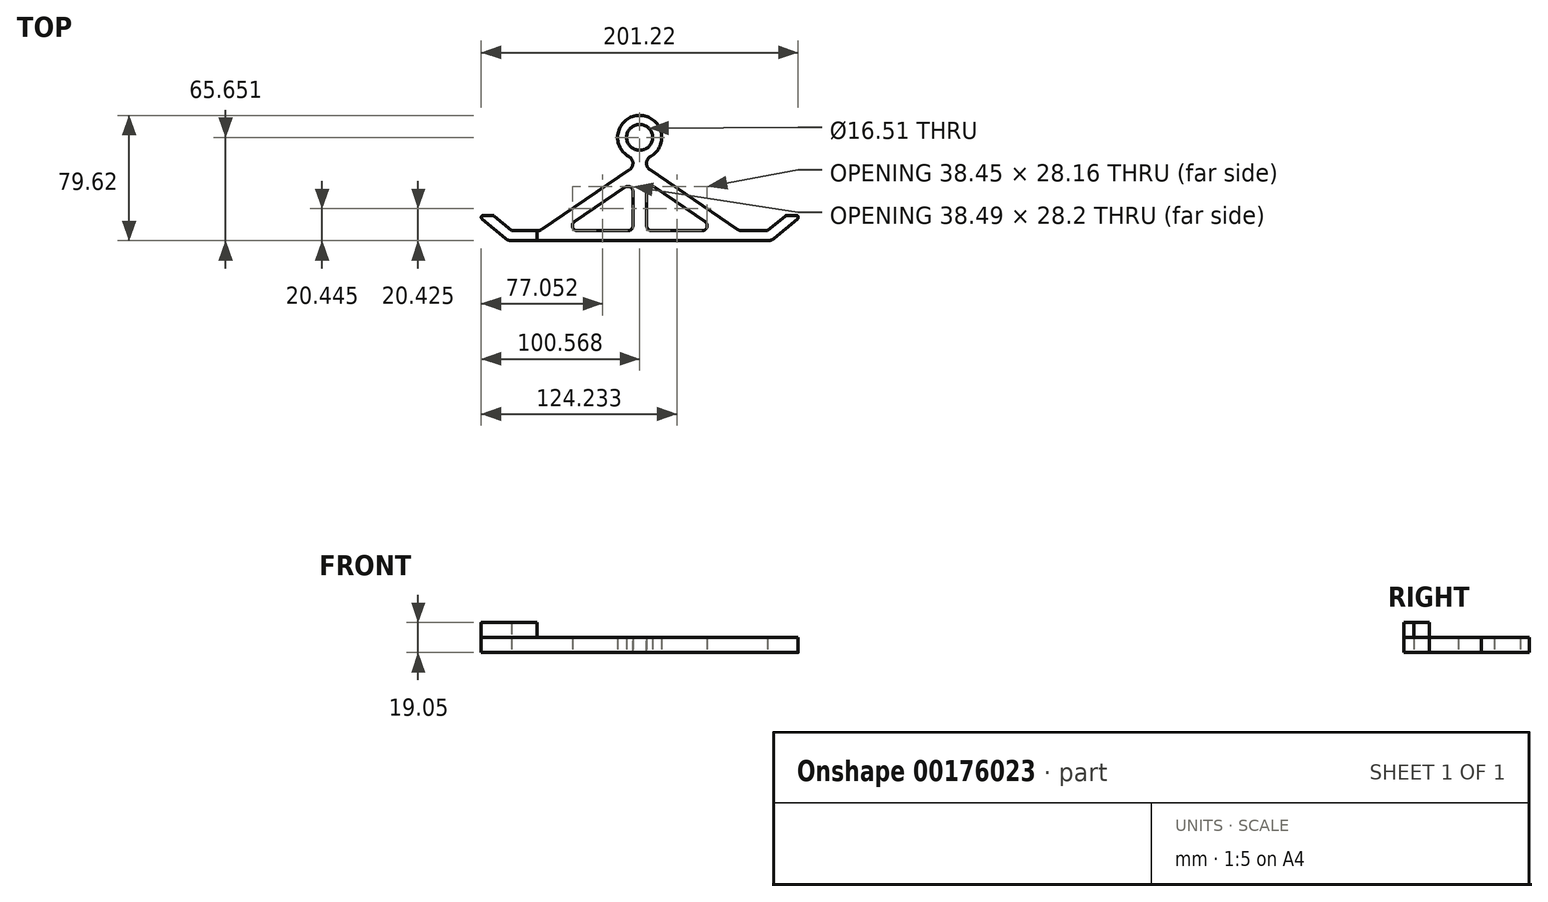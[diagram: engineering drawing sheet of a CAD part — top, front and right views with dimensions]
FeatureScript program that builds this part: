
annotation { "Feature Type Name" : "Feature", "Feature Type Description" : "" }
export const myFeature = defineFeature(function(context is Context, id is Id, definition is map)
    precondition{}
    {
        {
            var Q0;
            Q0=qCreatedBy(makeId("Top.planeOp"),FACE);
            var sketch = newSketch(context, id + "F0", { "sketchPlane" : qUnion([Q0])});
            skPoint(sketch, "E0", {"position": v(0, 0) * mm});
            skLineSegment(sketch, "E1.bottom", {"start": v(-4.4, 50.8) * mm, "end": v(4.31, 50.8) * mm, "construction": true});
            skLineSegment(sketch, "E1.left", {"start": v(-4.31, 16.52) * mm, "end": v(-4.31, -5.33) * mm});
            skLineSegment(sketch, "E1.right", {"start": v(4.4, 16.5) * mm, "end": v(4.4, -5.35) * mm});
            skPoint(sketch, "E1.top.end.orphan", {"position": v(4.4, -50.8) * mm});
            skPoint(sketch, "E1.top.start.orphan", {"position": v(-4.31, -50.8) * mm});
            skCircle(sketch, "E2", {"center": v(-0.04, 50.8) * mm, "radius": 13.97 * mm});
            skCircle(sketch, "E3", {"center": v(-0.04, 50.8) * mm, "radius": 8.26 * mm});
            skPoint(sketch, "E4", {"position": v(0, -8.58) * mm});
            skLineSegment(sketch, "E5", {"start": v(-39.63, -8.5) * mm, "end": v(-7.49, -8.5) * mm});
            skLineSegment(sketch, "E6", {"start": v(-63.5, -8.5) * mm, "end": v(-4.31, 31.74) * mm});
            skLineSegment(sketch, "E7", {"start": v(-9.27, 19.15) * mm, "end": v(-41.42, -2.7) * mm});
            skLineSegment(sketch, "E8.MirrorCS", {"start": v(63.5, -8.5) * mm, "end": v(4.31, 31.74) * mm});
            skLineSegment(sketch, "E9.MirrorCS", {"start": v(9.33, 19.11) * mm, "end": v(41.47, -2.74) * mm});
            skArc(sketch, "E10.filletArc", {"start": v(-4.31, 16.52) * mm, "mid": v(-6, 19.33) * mm, "end": v(-9.27, 19.15) * mm});
            skArc(sketch, "E11.filletArc", {"start": v(9.33, 19.11) * mm, "mid": v(6.08, 19.3) * mm, "end": v(4.4, 16.5) * mm});
            skPoint(sketch, "E12.newPointA", {"position": v(-4.31, 0) * mm});
            skArc(sketch, "E12.filletArc", {"start": v(-7.49, -8.5) * mm, "mid": v(-5.24, -7.57) * mm, "end": v(-4.31, -5.33) * mm});
            skArc(sketch, "E13.filletArc", {"start": v(-41.42, -2.7) * mm, "mid": v(-42.66, -6.26) * mm, "end": v(-39.63, -8.5) * mm});
            skLineSegment(sketch, "E14", {"start": v(39.7, -8.5) * mm, "end": v(7.55, -8.5) * mm});
            skLineSegment(sketch, "E15", {"start": v(-4.31, 31.74) * mm, "end": v(-4.34, 37.5) * mm});
            skLineSegment(sketch, "E16", {"start": v(4.31, 31.74) * mm, "end": v(4.31, 37.53) * mm});
            skArc(sketch, "E17.filletArc", {"start": v(39.7, -8.5) * mm, "mid": v(42.71, -6.28) * mm, "end": v(41.47, -2.74) * mm});
            skPoint(sketch, "E18.newPointA", {"position": v(4.4, 0) * mm});
            skArc(sketch, "E18.filletArc", {"start": v(4.4, -5.35) * mm, "mid": v(5.32, -7.58) * mm, "end": v(7.55, -8.5) * mm});
            skLineSegment(sketch, "E19", {"start": v(-63.5, -8.5) * mm, "end": v(-81.28, -8.5) * mm});
            skLineSegment(sketch, "E20", {"start": v(0, 39.41) * mm, "end": v(0, 0) * mm, "construction": true});
            skLineSegment(sketch, "E21.trimOffspring", {"start": v(-81.28, -14.85) * mm, "end": v(55.7, -14.85) * mm});
            skLineSegment(sketch, "E22.top", {"start": v(-93.42, 1.3) * mm, "end": v(-99.34, 1.3) * mm});
            skLineSegment(sketch, "E22.right", {"start": v(-85.36, -13.37) * mm, "end": v(-100.16, -0.95) * mm});
            skLineSegment(sketch, "E23.trimOffspring", {"start": v(-81.28, -8.5) * mm, "end": v(-92.6, 1) * mm});
            skArc(sketch, "E24.filletArc", {"start": v(-85.36, -13.37) * mm, "mid": v(-83.45, -14.47) * mm, "end": v(-81.28, -14.85) * mm});
            skArc(sketch, "E25.MirrorCS", {"start": v(85.36, -13.37) * mm, "mid": v(83.45, -14.47) * mm, "end": v(81.28, -14.85) * mm});
            skLineSegment(sketch, "E26.MirrorCS", {"start": v(63.5, -8.5) * mm, "end": v(81.28, -8.5) * mm});
            skLineSegment(sketch, "E27", {"start": v(55.7, -14.85) * mm, "end": v(81.28, -14.85) * mm});
            skPoint(sketch, "E28.visualSharp", {"position": v(-102.83, 1.3) * mm});
            skArc(sketch, "E28.filletArc", {"start": v(-99.34, 1.3) * mm, "mid": v(-100.54, 0.46) * mm, "end": v(-100.16, -0.95) * mm});
            skPoint(sketch, "E29.visualSharp", {"position": v(-92.95, 1.3) * mm});
            skArc(sketch, "E29.filletArc", {"start": v(-92.6, 1) * mm, "mid": v(-92.98, 1.22) * mm, "end": v(-93.42, 1.3) * mm});
            skLineSegment(sketch, "E30", {"start": v(-39.63, -8.5) * mm, "end": v(34.93, -8.5) * mm, "construction": true});
            skLineSegment(sketch, "E31.MirrorCS", {"start": v(93.42, 1.3) * mm, "end": v(99.34, 1.3) * mm});
            skPoint(sketch, "E32.MirrorP", {"position": v(102.83, 1.3) * mm});
            skArc(sketch, "E33.MirrorCS", {"start": v(99.34, 1.3) * mm, "mid": v(100.54, 0.46) * mm, "end": v(100.16, -0.95) * mm});
            skArc(sketch, "E34.MirrorCS", {"start": v(92.6, 1) * mm, "mid": v(92.98, 1.22) * mm, "end": v(93.42, 1.3) * mm});
            skLineSegment(sketch, "E35.MirrorCS", {"start": v(85.36, -13.37) * mm, "end": v(100.16, -0.95) * mm});
            skLineSegment(sketch, "E36", {"start": v(81.28, -8.5) * mm, "end": v(92.6, 1) * mm});
            skLineSegment(sketch, "E37", {"start": v(-92.6, 1) * mm, "end": v(-63.5, -8.5) * mm, "construction": true});
            skSolve(sketch);
        }
        {
            var Q0;
            {var subQ0=sQuery(id+"F0.wireOp",EDGE,"ZexEtosO-gTzE-p1Zg-nhXd-q58sbB5ociYp.bottom");Q0=makeQuery(id+"F0.imprint","IMPRINT",FACE,{"disambiguationData":[TD([[makeQuery(id+"F0.imprint","IMPRINT",EDGE,{"derivedFrom":subQ0}),1.0]])]});}
            var Q1;
            {var subQ0=sQuery(id+"F0.wireOp",EDGE,"2e53ea64-962b-49b4-b4d1-ffb74e6b5b81.trimOffspring");Q1=makeQuery(id+"F0.imprint","IMPRINT",FACE,{"disambiguationData":[TD([[makeQuery(id+"F0.imprint","IMPRINT",EDGE,{"derivedFrom":subQ0}),1.0]])]});}
            var Q2;
            {var subQ0=sQuery(id+"F0.wireOp",EDGE,"E2");var subQ1=sQuery(id+"F0.wireOp",EDGE,"E1.left");var subQ2=makeQuery(id+"F0.imprint","INTERSECT",VERTEX,{"derivedFrom":[subQ1,subQ0]});Q2=makeQuery(id+"F0.imprint","IMPRINT",FACE,{"disambiguationData":[TD([[makeQuery(id+"F0.imprint","IMPRINT",EDGE,{"disambiguationData":[TD([[subQ2,1.0]])],"derivedFrom":subQ1}),1.0]])]});}
            var Q3;
            {var subQ0=sQuery(id+"F0.wireOp",EDGE,"E8.MirrorCS");Q3=makeQuery(id+"F0.imprint","IMPRINT",FACE,{"disambiguationData":[TD([[makeQuery(id+"F0.imprint","IMPRINT",EDGE,{"derivedFrom":subQ0}),1.0]])]});}
            var Q4;
            {var subQ0=sQuery(id+"F0.wireOp",EDGE,"E6");Q4=makeQuery(id+"F0.imprint","IMPRINT",FACE,{"disambiguationData":[TD([[makeQuery(id+"F0.imprint","IMPRINT",EDGE,{"derivedFrom":subQ0}),-1.0]])]});}
            var Q5;
            {var subQ10=sQuery(id+"F0.wireOp",EDGE,"qVCZyQwn-OtZ2-INnO-DTXz-a9Wi9SraiNLx");Q5=makeQuery(id+"F0.imprint","IMPRINT",FACE,{"disambiguationData":[TD([[makeQuery(id+"F0.imprint","IMPRINT",EDGE,{"derivedFrom":subQ10}),1.0]])]});}
            var Q6;
            {var subQ7=sQuery(id+"F0.wireOp",EDGE,"ZexEtosO-gTzE-p1Zg-nhXd-q58sbB5ociYp.bottom");Q6=makeQuery(id+"F0.imprint","IMPRINT",FACE,{"disambiguationData":[TD([[makeQuery(id+"F0.imprint","IMPRINT",EDGE,{"derivedFrom":subQ7}),-1.0]])]});}
            var Q7;
            {var subQ0=sQuery(id+"F0.wireOp",EDGE,"E15");var subQ1=sQuery(id+"F0.wireOp",EDGE,"E2");var subQ2=makeQuery(id+"F0.imprint","INTERSECT",VERTEX,{"derivedFrom":[subQ1,subQ0]});Q7=makeQuery(id+"F0.imprint","IMPRINT",FACE,{"disambiguationData":[TD([[makeQuery(id+"F0.imprint","IMPRINT",EDGE,{"disambiguationData":[TD([[subQ2,1.0]])],"derivedFrom":subQ1}),1.0]])]});}
            var Q8;
            {var subQ0=sQuery(id+"F0.wireOp",EDGE,"E15");var subQ1=sQuery(id+"F0.wireOp",EDGE,"E2");var subQ2=makeQuery(id+"F0.imprint","INTERSECT",VERTEX,{"derivedFrom":[subQ1,subQ0]});Q8=makeQuery(id+"F0.imprint","IMPRINT",FACE,{"disambiguationData":[TD([[makeQuery(id+"F0.imprint","IMPRINT",EDGE,{"disambiguationData":[TD([[subQ2,-1.0]])],"derivedFrom":subQ1}),1.0]])]});}
            var Q9;
            Q9=makeQuery(id+"F0.imprint","IMPRINT",FACE,{"disambiguationData":[TD([[makeQuery(id+"F0.imprint","IMPRINT",EDGE,{"derivedFrom":sQuery(id+"F0.wireOp",EDGE,"WSke1GzU-CT4V-jziX-Hwsj-672698XO8zJv")}),1.0]])]});
            var Q10;
            {var subQ0=sQuery(id+"F0.wireOp",EDGE,"CPZqvH5Y-BvaM-udpB-Io5L-UT4IPwSyf7Zj");var subQ1=sQuery(id+"F0.wireOp",EDGE,"Tc2SKYOe-O6hR-xbep-DFvJ-nYTf5f4U04Ya");var subQ2=makeQuery(id+"F0.imprint","INTERSECT",VERTEX,{"derivedFrom":[subQ1,subQ0]});Q10=makeQuery(id+"F0.imprint","IMPRINT",FACE,{"disambiguationData":[TD([[makeQuery(id+"F0.imprint","IMPRINT",EDGE,{"disambiguationData":[TD([[subQ2,-1.0]])],"derivedFrom":subQ1}),1.0]])]});}
            var Q11;
            Q11=makeQuery(id+"F0.imprint","IMPRINT",FACE,{"disambiguationData":[TD([[makeQuery(id+"F0.imprint","IMPRINT",EDGE,{"derivedFrom":sQuery(id+"F0.wireOp",EDGE,"UfN6g7eB-UeiR-KPUq-fzXw-mm81oMTy26zH")}),-1.0]])]});
            var Q12;
            {var subQ0=sQuery(id+"F0.wireOp",EDGE,"172eb424-350f-45fe-882f-32ef7c5a9c630.MirrorCS");var subQ5=sQuery(id+"F0.wireOp",EDGE,"EjPThNtW-9Yum-e1bD-DIpl-6jBHqT7XyP80");var subQ6=makeQuery(id+"F0.imprint","INTERSECT",VERTEX,{"derivedFrom":[subQ5,subQ0]});Q12=makeQuery(id+"F0.imprint","IMPRINT",FACE,{"disambiguationData":[TD([[makeQuery(id+"F0.imprint","IMPRINT",EDGE,{"disambiguationData":[TD([[subQ6,1.0]])],"derivedFrom":subQ5}),-1.0]])]});}
            var Q13;
            {var subQ1=sQuery(id+"F0.wireOp",EDGE,"ZexEtosO-gTzE-p1Zg-nhXd-q58sbB5ociYp.top");var subQ3=sQuery(id+"F0.wireOp",EDGE,"1866efd8-0531-4193-b1c3-85d8478892f00.MirrorCS");var subQ4=makeQuery(id+"F0.imprint","INTERSECT",VERTEX,{"derivedFrom":[subQ1,subQ3]});Q13=makeQuery(id+"F0.imprint","IMPRINT",FACE,{"disambiguationData":[TD([[makeQuery(id+"F0.imprint","IMPRINT",EDGE,{"disambiguationData":[TD([[subQ4,-1.0]])],"derivedFrom":subQ3}),-1.0]])]});}
            var Q14;
            {var subQ3=sQuery(id+"F0.wireOp",EDGE,"1866efd8-0531-4193-b1c3-85d8478892f00.MirrorCS");var subQ5=sQuery(id+"F0.wireOp",EDGE,"2e53ea64-962b-49b4-b4d1-ffb74e6b5b81.trimOffspring");var subQ6=makeQuery(id+"F0.imprint","INTERSECT",VERTEX,{"derivedFrom":[subQ5,subQ3]});Q14=makeQuery(id+"F0.imprint","IMPRINT",FACE,{"disambiguationData":[TD([[makeQuery(id+"F0.imprint","IMPRINT",EDGE,{"disambiguationData":[TD([[subQ6,1.0]])],"derivedFrom":subQ5}),-1.0]])]});}
            var Q15;
            Q15=makeQuery(id+"F0.imprint","IMPRINT",FACE,{"disambiguationData":[TD([[makeQuery(id+"F0.imprint","IMPRINT",EDGE,{"derivedFrom":sQuery(id+"F0.wireOp",EDGE,"6ab3470a-25a7-409c-98cc-0288ee2b45f90.MirrorCS")}),-1.0]])]});
            var Q16;
            Q16=makeQuery(id+"F0.imprint","IMPRINT",FACE,{"disambiguationData":[TD([[makeQuery(id+"F0.imprint","IMPRINT",EDGE,{"derivedFrom":sQuery(id+"F0.wireOp",EDGE,"03efa375-6f5e-4061-832d-d3cbae6344830.MirrorCS")}),1.0]])]});
            var Q17;
            Q17=makeQuery(id+"F0.imprint","IMPRINT",FACE,{"disambiguationData":[TD([[makeQuery(id+"F0.imprint","IMPRINT",EDGE,{"derivedFrom":sQuery(id+"F0.wireOp",EDGE,"ZBMSd0vS-CLQh-kAwR-065j-9fsP6c82n6la")}),-1.0]])]});
            var Q18;
            Q18=makeQuery(id+"F0.imprint","IMPRINT",FACE,{"disambiguationData":[TD([[makeQuery(id+"F0.imprint","IMPRINT",EDGE,{"derivedFrom":sQuery(id+"F0.wireOp",EDGE,"99367227-8b72-4382-abf1-aa9aecd7a6840.MirrorCS")}),1.0]])]});
            extrude(context, id + "F1", {"entities" : qUnion([Q0, Q1, Q2, Q3, Q4, Q5, Q6, Q7, Q8, Q9, Q10, Q11, Q12, Q13, Q14, Q15, Q16, Q17, Q18]), "depth" : 9.52 * mm});
        }
        {
            var Q0;
            Q0=makeQuery(id+"F1.opExtrude","SWEPT_EDGE",EDGE,{"disambiguationData":[OSD([sQuery(id+"F0.wireOp",EDGE,"E8.MirrorCS"),sQuery(id+"F0.wireOp",EDGE,"E16")])]});
            var Q1;
            Q1=makeQuery(id+"F1.opExtrude","SWEPT_EDGE",EDGE,{"disambiguationData":[OSD([sQuery(id+"F0.wireOp",EDGE,"E2"),sQuery(id+"F0.wireOp",EDGE,"E16")])]});
            var Q2;
            Q2=makeQuery(id+"F1.opExtrude","SWEPT_EDGE",EDGE,{"disambiguationData":[OSD([sQuery(id+"F0.wireOp",EDGE,"E6"),sQuery(id+"F0.wireOp",EDGE,"E15")])]});
            var Q3;
            Q3=makeQuery(id+"F1.opExtrude","SWEPT_EDGE",EDGE,{"disambiguationData":[OSD([sQuery(id+"F0.wireOp",EDGE,"E2"),sQuery(id+"F0.wireOp",EDGE,"E15")])]});
            var Q4;
            Q4=makeQuery(id+"F1.opExtrude","SWEPT_EDGE",EDGE,{"disambiguationData":[OSD([sQuery(id+"F0.wireOp",EDGE,"E6"),sQuery(id+"F0.wireOp",EDGE,"j4BW1nc1-JnIR-nkPM-GjxP-GzGe1Y6KnPiL")])]});
            var Q5;
            Q5=makeQuery(id+"F1.opExtrude","SWEPT_EDGE",EDGE,{"disambiguationData":[OSD([sQuery(id+"F0.wireOp",EDGE,"E8.MirrorCS"),sQuery(id+"F0.wireOp",EDGE,"EjPThNtW-9Yum-e1bD-DIpl-6jBHqT7XyP80")])]});
            fillet(context, id + "F2", {"entities" : qUnion([Q0, Q1, Q2, Q3, Q4, Q5]), "radius" : 5.08 * mm, "tangentPropagation" : true, "allowEdgeOverflow" : false});
        }
        {
            var Q0;
            Q0=makeQuery(id+"F1.opExtrude","CAP_FACE",FACE,{"disambiguationData":[OSD([sQuery(id+"F0.wireOp",EDGE,"E1.left"),sQuery(id+"F0.wireOp",EDGE,"E1.right"),sQuery(id+"F0.wireOp",EDGE,"E2"),sQuery(id+"F0.wireOp",EDGE,"E3"),sQuery(id+"F0.wireOp",EDGE,"E5"),sQuery(id+"F0.wireOp",EDGE,"E6"),sQuery(id+"F0.wireOp",EDGE,"E7"),sQuery(id+"F0.wireOp",EDGE,"E8.MirrorCS"),sQuery(id+"F0.wireOp",EDGE,"E9.MirrorCS"),sQuery(id+"F0.wireOp",EDGE,"E10.filletArc"),sQuery(id+"F0.wireOp",EDGE,"E11.filletArc"),sQuery(id+"F0.wireOp",EDGE,"E12.filletArc"),sQuery(id+"F0.wireOp",EDGE,"E13.filletArc"),sQuery(id+"F0.wireOp",EDGE,"E14"),sQuery(id+"F0.wireOp",EDGE,"E15"),sQuery(id+"F0.wireOp",EDGE,"E16"),sQuery(id+"F0.wireOp",EDGE,"E17.filletArc"),sQuery(id+"F0.wireOp",EDGE,"E18.filletArc"),sQuery(id+"F0.wireOp",EDGE,"E19"),sQuery(id+"F0.wireOp",EDGE,"E21.trimOffspring"),sQuery(id+"F0.wireOp",EDGE,"E22.top"),sQuery(id+"F0.wireOp",EDGE,"E22.right"),sQuery(id+"F0.wireOp",EDGE,"E23.trimOffspring"),sQuery(id+"F0.wireOp",EDGE,"E24.filletArc"),sQuery(id+"F0.wireOp",EDGE,"E25.MirrorCS"),sQuery(id+"F0.wireOp",EDGE,"E26.MirrorCS"),sQuery(id+"F0.wireOp",EDGE,"E27"),sQuery(id+"F0.wireOp",EDGE,"E28.filletArc"),sQuery(id+"F0.wireOp",EDGE,"E29.filletArc"),sQuery(id+"F0.wireOp",EDGE,"E31.MirrorCS"),sQuery(id+"F0.wireOp",EDGE,"E33.MirrorCS"),sQuery(id+"F0.wireOp",EDGE,"E34.MirrorCS"),sQuery(id+"F0.wireOp",EDGE,"E35.MirrorCS"),sQuery(id+"F0.wireOp",EDGE,"E36")])],"isStart":false});
            var sketch = newSketch(context, id + "F3", { "sketchPlane" : qUnion([Q0])});
            skLineSegment(sketch, "E38.0", {"start": v(-93.42, 1.3) * mm, "end": v(-99.34, 1.3) * mm});
            skLineSegment(sketch, "E38.1", {"start": v(-85.36, -13.37) * mm, "end": v(-100.16, -0.95) * mm});
            skArc(sketch, "E38.2", {"start": v(-99.34, 1.3) * mm, "mid": v(-100.54, 0.46) * mm, "end": v(-100.16, -0.95) * mm});
            skLineSegment(sketch, "E38.3", {"start": v(-81.28, -8.5) * mm, "end": v(-92.6, 1) * mm});
            skArc(sketch, "E38.4", {"start": v(-92.6, 1) * mm, "mid": v(-92.98, 1.22) * mm, "end": v(-93.42, 1.3) * mm});
            skArc(sketch, "E38.5", {"start": v(-85.36, -13.37) * mm, "mid": v(-83.45, -14.47) * mm, "end": v(-81.28, -14.85) * mm});
            skLineSegment(sketch, "E38.6", {"start": v(-65.06, -8.5) * mm, "end": v(-81.28, -8.5) * mm});
            skLineSegment(sketch, "E39", {"start": v(-81.28, -14.85) * mm, "end": v(-65.06, -14.85) * mm});
            skLineSegment(sketch, "E40", {"start": v(-65.06, -14.85) * mm, "end": v(-65.06, -8.5) * mm});
            skSolve(sketch);
        }
        {
            var Q0;
            Q0 = qSketchRegion(id + "F3", true);
            extrude(context, id + "F4", {"entities" : qUnion([Q0]), "depth" : 9.52 * mm});
        }
    });
